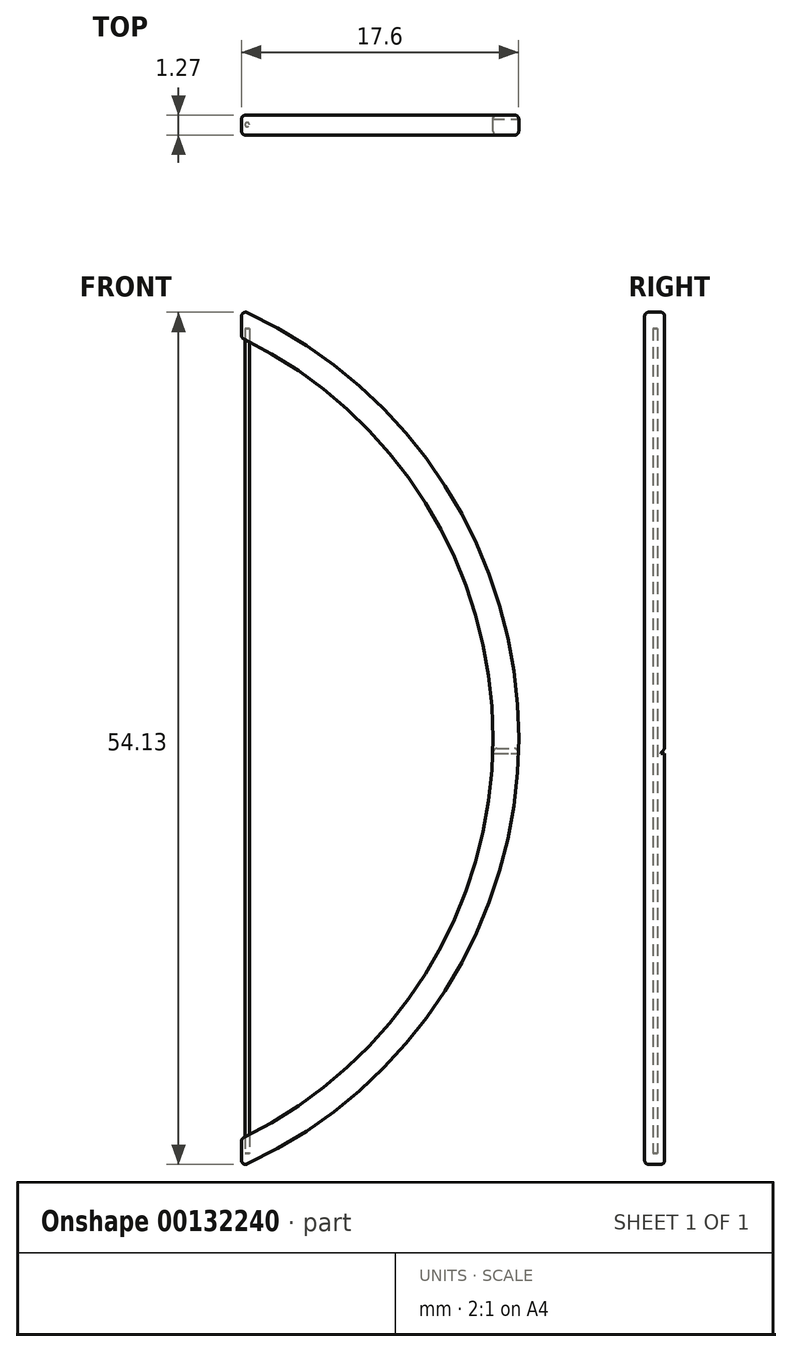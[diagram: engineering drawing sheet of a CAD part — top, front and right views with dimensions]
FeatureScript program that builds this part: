
annotation { "Feature Type Name" : "Feature", "Feature Type Description" : "" }
export const myFeature = defineFeature(function(context is Context, id is Id, definition is map)
    precondition{}
    {
        {
            var Q0;
            Q0=qCreatedBy(makeId("Front.planeOp"),FACE);
            var sketch = newSketch(context, id + "F0", { "sketchPlane" : qUnion([Q0])});
            skArc(sketch, "E0", {"start": v(0, -26.24) * mm, "mid": v(17.6, 0.96) * mm, "end": v(0, 28.17) * mm});
            skLineSegment(sketch, "E1", {"start": v(0, 28.17) * mm, "end": v(0, 26.4) * mm});
            skLineSegment(sketch, "E2", {"start": v(0, -26.24) * mm, "end": v(0, -24.46) * mm});
            skArc(sketch, "E3", {"start": v(0, -24.46) * mm, "mid": v(15.98, 0.96) * mm, "end": v(0, 26.4) * mm});
            skSolve(sketch);
        }
        {
            var Q0;
            Q0 = qSketchRegion(id + "F0", true);
            extrude(context, id + "F1", {"entities" : qUnion([Q0]), "depth" : 1.27 * mm});
        }
        {
            var Q0;
            Q0=makeQuery(id+"F1.opExtrude","SWEPT_EDGE",EDGE,{"disambiguationData":[OSD([sQuery(id+"F0.wireOp",EDGE,"E1"),sQuery(id+"F0.wireOp",EDGE,"E3")])]});
            var Q1;
            Q1=makeQuery(id+"F1.opExtrude","CAP_EDGE",EDGE,{"disambiguationData":[OSD([sQuery(id+"F0.wireOp",EDGE,"E1")])],"isStart":false});
            var Q2;
            Q2=makeQuery(id+"F1.opExtrude","CAP_EDGE",EDGE,{"disambiguationData":[OSD([sQuery(id+"F0.wireOp",EDGE,"E1")])],"isStart":true});
            var Q3;
            Q3=makeQuery(id+"F1.opExtrude","SWEPT_EDGE",EDGE,{"disambiguationData":[OSD([sQuery(id+"F0.wireOp",EDGE,"E0"),sQuery(id+"F0.wireOp",EDGE,"E1")])]});
            var Q4;
            Q4=makeQuery(id+"F1.opExtrude","CAP_EDGE",EDGE,{"disambiguationData":[OSD([sQuery(id+"F0.wireOp",EDGE,"E0")])],"isStart":false});
            var Q5;
            Q5=makeQuery(id+"F1.opExtrude","CAP_EDGE",EDGE,{"disambiguationData":[OSD([sQuery(id+"F0.wireOp",EDGE,"E0")])],"isStart":true});
            var Q6;
            Q6=makeQuery(id+"F1.opExtrude","CAP_EDGE",EDGE,{"disambiguationData":[OSD([sQuery(id+"F0.wireOp",EDGE,"E3")])],"isStart":false});
            var Q7;
            Q7=makeQuery(id+"F1.opExtrude","CAP_EDGE",EDGE,{"disambiguationData":[OSD([sQuery(id+"F0.wireOp",EDGE,"E3")])],"isStart":true});
            var Q8;
            Q8=makeQuery(id+"F1.opExtrude","SWEPT_EDGE",EDGE,{"disambiguationData":[OSD([sQuery(id+"F0.wireOp",EDGE,"E2"),sQuery(id+"F0.wireOp",EDGE,"E3")])]});
            var Q9;
            Q9=makeQuery(id+"F1.opExtrude","CAP_EDGE",EDGE,{"disambiguationData":[OSD([sQuery(id+"F0.wireOp",EDGE,"E2")])],"isStart":true});
            var Q10;
            Q10=makeQuery(id+"F1.opExtrude","SWEPT_EDGE",EDGE,{"disambiguationData":[OSD([sQuery(id+"F0.wireOp",EDGE,"E0"),sQuery(id+"F0.wireOp",EDGE,"E2")])]});
            var Q11;
            Q11=makeQuery(id+"F1.opExtrude","CAP_EDGE",EDGE,{"disambiguationData":[OSD([sQuery(id+"F0.wireOp",EDGE,"E2")])],"isStart":false});
            fillet(context, id + "F2", {"entities" : qUnion([Q0, Q1, Q2, Q3, Q4, Q5, Q6, Q7, Q8, Q9, Q10, Q11]), "radius" : 0.25 * mm, "tangentPropagation" : true, "allowEdgeOverflow" : false});
        }
        {
            var Q0;
            Q0=qCreatedBy(makeId("Top.planeOp"),FACE);
            var sketch = newSketch(context, id + "F3", { "sketchPlane" : qUnion([Q0])});
            skCircle(sketch, "E4", {"center": v(0.36, -0.6) * mm, "radius": 0.14 * mm});
            skSolve(sketch);
        }
        {
            var Q0;
            Q0 = qSketchRegion(id + "F3", true);
            extrude(context, id + "F4", {"entities" : qUnion([Q0]), "depth" : 26.98 * mm, "hasSecondDirection" : true, "secondDirectionOppositeDirection" : true, "secondDirectionDepth" : 25.4 * mm});
        }
        {
            var Q0;
            Q0=qCreatedBy(makeId("Right.planeOp"),FACE);
            var sketch = newSketch(context, id + "F5", { "sketchPlane" : qUnion([Q0])});
            skLineSegment(sketch, "E5", {"start": v(0, 0) * mm, "end": v(-0.25, 0) * mm});
            skLineSegment(sketch, "E6", {"start": v(-0.25, 0) * mm, "end": v(0, 0.32) * mm});
            skLineSegment(sketch, "E7", {"start": v(0, 0.32) * mm, "end": v(0, 0) * mm});
            skSolve(sketch);
        }
        {
            var Q0;
            Q0 = qSketchRegion(id + "F5", true);
            extrude(context, id + "F6", {"entities" : qUnion([Q0]), "operationType" : NewBodyOperationType.REMOVE, "oppositeDirection" : true, "depth" : 25.4 * mm, "hasSecondDirection" : true, "secondDirectionOppositeDirection" : false, "secondDirectionDepth" : 25.4 * mm});
        }
    });
